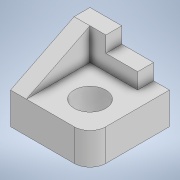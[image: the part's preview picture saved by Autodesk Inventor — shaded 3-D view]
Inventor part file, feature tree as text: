
AUTODESK INVENTOR PART (.ipt)
format: ipt  version: 2020 (Build 240168000, 168)  size: 140,800 bytes
history: native  units: mm
features: extrude x5, sketch x5, other x1, fillet x1
ambient origin geometry x8: Origin, YZ Plane, XZ Plane, XY Plane, X Axis, Y Axis, Z Axis, Center Point
bodies: Body1 (feature_tree)
feature tree (12):
  other  "實體1"
  extrude  "擠出1"  Depth=20.0mm
  extrude  "擠出2"  Depth=50.0mm
  extrude  "擠出3"  Depth=50.0mm TaperAngle=0.0deg
  extrude  "擠出4"  Depth=40.0mm
  extrude  "擠出5"  Depth=10.0mm
  fillet  "圓角1"  Radius=20.0mm
  sketch  "草圖1"
  sketch  "草圖2"
  sketch  "草圖3"
  sketch  "草圖4"
  sketch  "草圖5"
